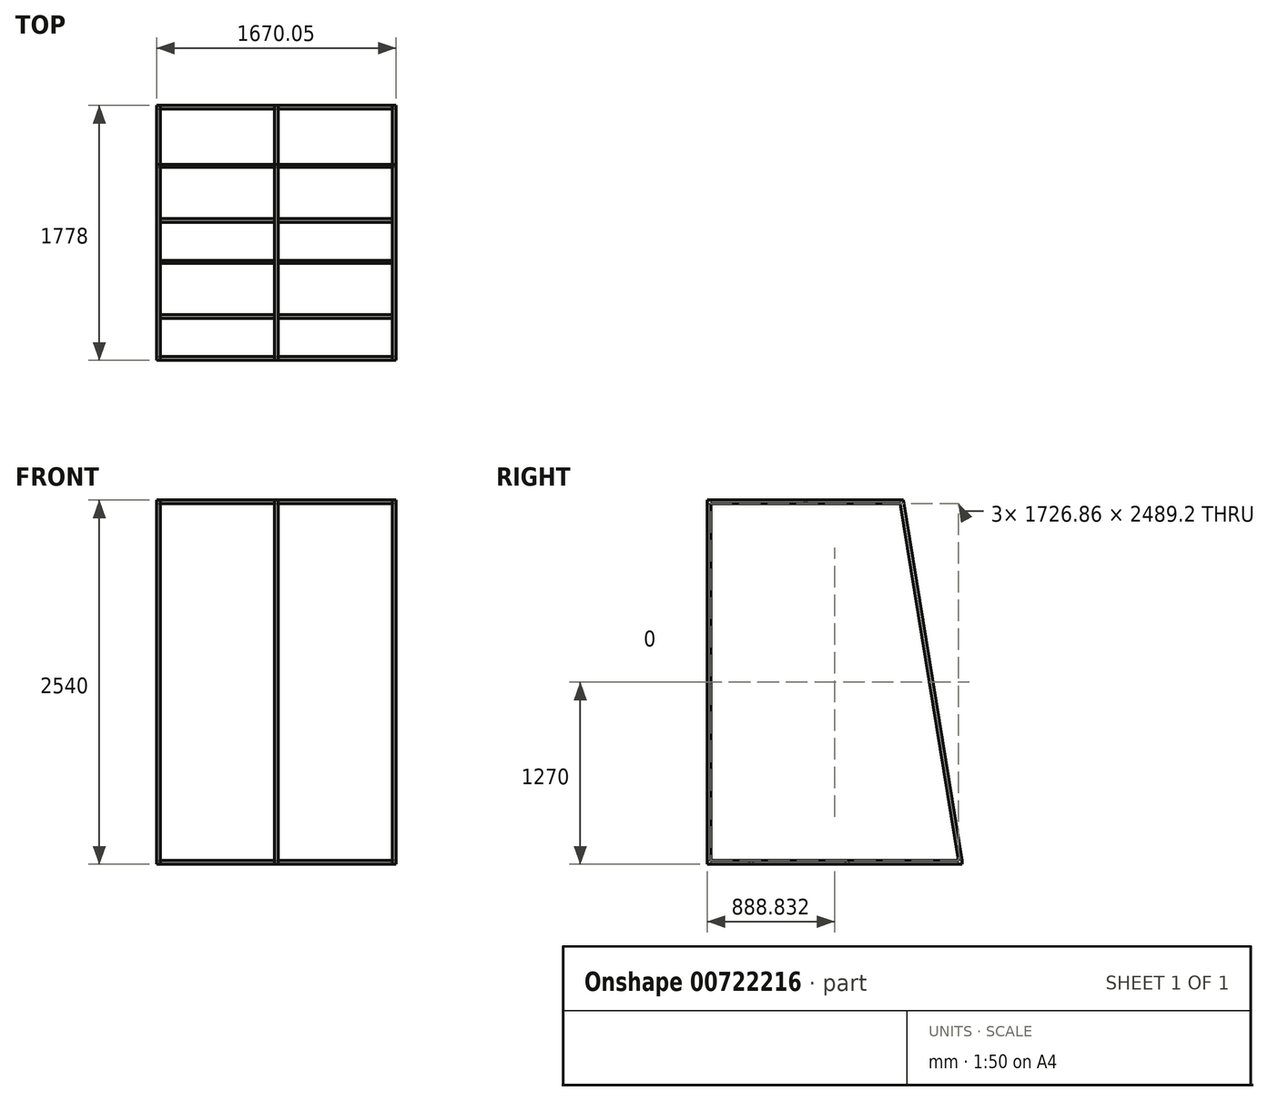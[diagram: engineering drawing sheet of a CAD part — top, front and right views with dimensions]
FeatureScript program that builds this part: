
annotation { "Feature Type Name" : "Feature", "Feature Type Description" : "" }
export const myFeature = defineFeature(function(context is Context, id is Id, definition is map)
    precondition{}
    {
        {
            var Q0;
            Q0=qCreatedBy(makeId("Right.planeOp"),FACE);
            var sketch = newSketch(context, id + "F0", { "sketchPlane" : qUnion([Q0])});
            skLineSegment(sketch, "E0.bottom", {"start": v(0, 0) * mm, "end": v(25.4, 0) * mm});
            skLineSegment(sketch, "E0.top", {"start": v(0, 2489.2) * mm, "end": v(25.4, 2489.2) * mm});
            skLineSegment(sketch, "E0.left", {"start": v(0, 0) * mm, "end": v(0, 2489.2) * mm});
            skLineSegment(sketch, "E0.right", {"start": v(25.4, 0) * mm, "end": v(25.4, 2489.2) * mm});
            skLineSegment(sketch, "E1.bottom", {"start": v(0, 0) * mm, "end": v(1778, 0) * mm});
            skLineSegment(sketch, "E1.top", {"start": v(0, -25.4) * mm, "end": v(1778, -25.4) * mm});
            skLineSegment(sketch, "E1.left", {"start": v(0, 0) * mm, "end": v(0, -25.4) * mm});
            skLineSegment(sketch, "E1.right", {"start": v(1778, 0) * mm, "end": v(1778, -25.4) * mm});
            skLineSegment(sketch, "E2.bottom", {"start": v(0, 2489.2) * mm, "end": v(1371.6, 2489.2) * mm});
            skLineSegment(sketch, "E2.top", {"start": v(0, 2514.6) * mm, "end": v(1367.45, 2514.6) * mm});
            skLineSegment(sketch, "E2.left", {"start": v(0, 2489.2) * mm, "end": v(0, 2514.6) * mm});
            skLineSegment(sketch, "E3", {"start": v(1778, 0) * mm, "end": v(1367.45, 2514.6) * mm});
            skLineSegment(sketch, "E4.0", {"start": v(1752.26, 0) * mm, "end": v(1345.86, 2489.2) * mm});
            skLineSegment(sketch, "E5.bottom", {"start": v(673.1, 2489.2) * mm, "end": v(698.5, 2489.2) * mm});
            skLineSegment(sketch, "E5.top", {"start": v(673.1, 0) * mm, "end": v(698.5, 0) * mm});
            skLineSegment(sketch, "E5.left", {"start": v(673.1, 2489.2) * mm, "end": v(673.1, 0) * mm});
            skLineSegment(sketch, "E5.right", {"start": v(698.5, 2489.2) * mm, "end": v(698.5, 0) * mm});
            skSolve(sketch);
        }
        {
            var Q0;
            Q0 = qSketchRegion(id + "F0", true);
            var Q1;
            Q1=makeQuery(id+"F0.imprint","IMPRINT",FACE,{"disambiguationData":[TD([[makeQuery(id+"F0.imprint","IMPRINT",EDGE,{"derivedFrom":sQuery(id+"F0.wireOp",EDGE,"E5.bottom")}),-1.0]])]});
            extrude(context, id + "F1", {"entities" : qUnion([Q0, Q1]), "depth" : 25.4 * mm, "offsetDistance" : 25.4 * mm});
        }
        {
            var Q0;
            Q0=makeQuery(id+"F1.opExtrude","CAP_FACE",FACE,{"disambiguationData":[OSD([sQuery(id+"F0.wireOp",EDGE,"E0.left"),sQuery(id+"F0.wireOp",EDGE,"E0.right"),sQuery(id+"F0.wireOp",EDGE,"E1.bottom"),sQuery(id+"F0.wireOp",EDGE,"E1.top"),sQuery(id+"F0.wireOp",EDGE,"E1.left"),sQuery(id+"F0.wireOp",EDGE,"E1.right"),sQuery(id+"F0.wireOp",EDGE,"E2.bottom"),sQuery(id+"F0.wireOp",EDGE,"E2.top"),sQuery(id+"F0.wireOp",EDGE,"E2.left"),sQuery(id+"F0.wireOp",EDGE,"E3"),sQuery(id+"F0.wireOp",EDGE,"E4.0"),sQuery(id+"F0.wireOp",EDGE,"E5.left"),sQuery(id+"F0.wireOp",EDGE,"E5.right")])],"isStart":false});
            cPlane(context, id + "F2", {"entities" : qUnion([Q0]), "cplaneType" : CPlaneType.OFFSET, "offset" : 835.02 * mm, "oppositeDirection" : true, "width" : 152.4 * mm, "height" : 152.4 * mm});
        }
        {
            var Q0;
            Q0=makeQuery(id+"F1.opExtrude","SWEPT_BODY",BODY,{"disambiguationData":[OSD([sQuery(id+"F0.wireOp",EDGE,"E0.left"),sQuery(id+"F0.wireOp",EDGE,"E0.right"),sQuery(id+"F0.wireOp",EDGE,"E1.bottom"),sQuery(id+"F0.wireOp",EDGE,"E1.top"),sQuery(id+"F0.wireOp",EDGE,"E1.left"),sQuery(id+"F0.wireOp",EDGE,"E1.right"),sQuery(id+"F0.wireOp",EDGE,"E2.bottom"),sQuery(id+"F0.wireOp",EDGE,"E2.top"),sQuery(id+"F0.wireOp",EDGE,"E2.left"),sQuery(id+"F0.wireOp",EDGE,"E3"),sQuery(id+"F0.wireOp",EDGE,"E4.0"),sQuery(id+"F0.wireOp",EDGE,"E5.left"),sQuery(id+"F0.wireOp",EDGE,"E5.right")])]});
            var Q1;
            Q1=qCreatedBy(id+"F2.planeOp",FACE);
            mirror(context, id + "F3", {"entities" : qUnion([Q0]), "mirrorPlane" : qUnion([Q1])});
        }
        {
            var Q0;
            Q0=makeQuery(id+"F1.opExtrude","CAP_FACE",FACE,{"disambiguationData":[OSD([sQuery(id+"F0.wireOp",EDGE,"E0.left"),sQuery(id+"F0.wireOp",EDGE,"E0.right"),sQuery(id+"F0.wireOp",EDGE,"E1.bottom"),sQuery(id+"F0.wireOp",EDGE,"E1.top"),sQuery(id+"F0.wireOp",EDGE,"E1.left"),sQuery(id+"F0.wireOp",EDGE,"E1.right"),sQuery(id+"F0.wireOp",EDGE,"E2.bottom"),sQuery(id+"F0.wireOp",EDGE,"E2.top"),sQuery(id+"F0.wireOp",EDGE,"E2.left"),sQuery(id+"F0.wireOp",EDGE,"E3"),sQuery(id+"F0.wireOp",EDGE,"E4.0"),sQuery(id+"F0.wireOp",EDGE,"E5.left"),sQuery(id+"F0.wireOp",EDGE,"E5.right")])],"isStart":false});
            cPlane(context, id + "F4", {"entities" : qUnion([Q0]), "cplaneType" : CPlaneType.OFFSET, "offset" : 423.86 * mm, "oppositeDirection" : true, "width" : 152.4 * mm, "height" : 152.4 * mm});
        }
        {
            var Q0;
            Q0=makeQuery(id+"F1.opExtrude","SWEPT_BODY",BODY,{"disambiguationData":[OSD([sQuery(id+"F0.wireOp",EDGE,"E0.left"),sQuery(id+"F0.wireOp",EDGE,"E0.right"),sQuery(id+"F0.wireOp",EDGE,"E1.bottom"),sQuery(id+"F0.wireOp",EDGE,"E1.top"),sQuery(id+"F0.wireOp",EDGE,"E1.left"),sQuery(id+"F0.wireOp",EDGE,"E1.right"),sQuery(id+"F0.wireOp",EDGE,"E2.bottom"),sQuery(id+"F0.wireOp",EDGE,"E2.top"),sQuery(id+"F0.wireOp",EDGE,"E2.left"),sQuery(id+"F0.wireOp",EDGE,"E3"),sQuery(id+"F0.wireOp",EDGE,"E4.0"),sQuery(id+"F0.wireOp",EDGE,"E5.left"),sQuery(id+"F0.wireOp",EDGE,"E5.right")])]});
            var Q1;
            Q1=qCreatedBy(id+"F4.planeOp",FACE);
            mirror(context, id + "F5", {"entities" : qUnion([Q0]), "mirrorPlane" : qUnion([Q1])});
        }
        {
            var Q0;
            Q0=makeQuery(id+"F5.opPattern","COPY",FACE,{"derivedFrom":makeQuery(id+"F1.opExtrude","CAP_FACE",FACE,{"disambiguationData":[OSD([sQuery(id+"F0.wireOp",EDGE,"E0.left"),sQuery(id+"F0.wireOp",EDGE,"E0.right"),sQuery(id+"F0.wireOp",EDGE,"E1.bottom"),sQuery(id+"F0.wireOp",EDGE,"E1.top"),sQuery(id+"F0.wireOp",EDGE,"E1.left"),sQuery(id+"F0.wireOp",EDGE,"E1.right"),sQuery(id+"F0.wireOp",EDGE,"E2.bottom"),sQuery(id+"F0.wireOp",EDGE,"E2.top"),sQuery(id+"F0.wireOp",EDGE,"E2.left"),sQuery(id+"F0.wireOp",EDGE,"E3"),sQuery(id+"F0.wireOp",EDGE,"E4.0"),sQuery(id+"F0.wireOp",EDGE,"E5.left"),sQuery(id+"F0.wireOp",EDGE,"E5.right")])],"isStart":true}),"instanceName":"1"});
            var sketch = newSketch(context, id + "F6", { "sketchPlane" : qUnion([Q0])});
            skLineSegment(sketch, "E6.bottom", {"start": v(1778, -25.4) * mm, "end": v(1752.6, -25.4) * mm});
            skLineSegment(sketch, "E6.top", {"start": v(1778, 0) * mm, "end": v(1752.6, 0) * mm});
            skLineSegment(sketch, "E6.left", {"start": v(1778, -25.4) * mm, "end": v(1778, 0) * mm});
            skLineSegment(sketch, "E6.right", {"start": v(1752.6, -25.4) * mm, "end": v(1752.6, 0) * mm});
            skLineSegment(sketch, "E7.bottom", {"start": v(0, -25.4) * mm, "end": v(25.4, -25.4) * mm});
            skLineSegment(sketch, "E7.top", {"start": v(0, 0) * mm, "end": v(25.4, 0) * mm});
            skLineSegment(sketch, "E7.left", {"start": v(0, -25.4) * mm, "end": v(0, 0) * mm});
            skLineSegment(sketch, "E7.right", {"start": v(25.4, -25.4) * mm, "end": v(25.4, 0) * mm});
            skLineSegment(sketch, "E8.bottom", {"start": v(0, 2514.6) * mm, "end": v(25.4, 2514.6) * mm});
            skLineSegment(sketch, "E8.top", {"start": v(0, 2489.2) * mm, "end": v(25.4, 2489.2) * mm});
            skLineSegment(sketch, "E8.left", {"start": v(0, 2514.6) * mm, "end": v(0, 2489.2) * mm});
            skLineSegment(sketch, "E8.right", {"start": v(25.4, 2514.6) * mm, "end": v(25.4, 2489.2) * mm});
            skLineSegment(sketch, "E9.bottom", {"start": v(292.1, 0) * mm, "end": v(317.5, 0) * mm});
            skLineSegment(sketch, "E9.top", {"start": v(292.1, -25.4) * mm, "end": v(317.5, -25.4) * mm});
            skLineSegment(sketch, "E9.left", {"start": v(292.1, 0) * mm, "end": v(292.1, -25.4) * mm});
            skLineSegment(sketch, "E9.right", {"start": v(317.5, 0) * mm, "end": v(317.5, -25.4) * mm});
            skLineSegment(sketch, "E10.bottom", {"start": v(962.03, 0) * mm, "end": v(987.43, 0) * mm});
            skLineSegment(sketch, "E10.top", {"start": v(962.03, -25.4) * mm, "end": v(987.43, -25.4) * mm});
            skLineSegment(sketch, "E10.left", {"start": v(962.03, 0) * mm, "end": v(962.03, -25.4) * mm});
            skLineSegment(sketch, "E10.right", {"start": v(987.43, 0) * mm, "end": v(987.43, -25.4) * mm});
            skPoint(sketch, "E11.centerSnap0", {"position": v(25.4, 2501.9) * mm});
            skLineSegment(sketch, "E12", {"start": v(673.1, 2489.2) * mm, "end": v(698.5, 2489.2) * mm, "construction": true});
            skCircle(sketch, "E13", {"center": v(685.8, 2501.9) * mm, "radius": 12.7 * mm, "construction": true});
            skPoint(sketch, "E13.centerSnap0", {"position": v(685.8, 2489.2) * mm});
            skCircle(sketch, "E14", {"center": v(1355.72, 2501.9) * mm, "radius": 12.7 * mm, "construction": true});
            skCircle(sketch, "E15", {"center": v(685.8, 2501.9) * mm, "radius": 9.53 * mm});
            skCircle(sketch, "E16", {"center": v(1355.72, 2501.9) * mm, "radius": 9.53 * mm});
            skSolve(sketch);
        }
        {
            var Q0;
            Q0 = qSketchRegion(id + "F6", true);
            var Q1;
            Q1=makeQuery(id+"F1.opExtrude","CAP_FACE",FACE,{"disambiguationData":[OSD([sQuery(id+"F0.wireOp",EDGE,"E0.left"),sQuery(id+"F0.wireOp",EDGE,"E0.right"),sQuery(id+"F0.wireOp",EDGE,"E1.bottom"),sQuery(id+"F0.wireOp",EDGE,"E1.top"),sQuery(id+"F0.wireOp",EDGE,"E1.left"),sQuery(id+"F0.wireOp",EDGE,"E1.right"),sQuery(id+"F0.wireOp",EDGE,"E2.bottom"),sQuery(id+"F0.wireOp",EDGE,"E2.top"),sQuery(id+"F0.wireOp",EDGE,"E2.left"),sQuery(id+"F0.wireOp",EDGE,"E3"),sQuery(id+"F0.wireOp",EDGE,"E4.0"),sQuery(id+"F0.wireOp",EDGE,"E5.left"),sQuery(id+"F0.wireOp",EDGE,"E5.right")])],"isStart":true});
            extrude(context, id + "F7", {"entities" : qUnion([Q0]), "endBound" : BoundingType.UP_TO_SURFACE, "depth" : 25.4 * mm, "endBoundEntityFace" : qUnion([Q1]), "offsetDistance" : 25.4 * mm});
        }
        {
            var Q0;
            Q0=makeQuery(id+"F5.opPattern","COPY",FACE,{"derivedFrom":makeQuery(id+"F1.opExtrude","CAP_FACE",FACE,{"disambiguationData":[OSD([sQuery(id+"F0.wireOp",EDGE,"E0.left"),sQuery(id+"F0.wireOp",EDGE,"E0.right"),sQuery(id+"F0.wireOp",EDGE,"E1.bottom"),sQuery(id+"F0.wireOp",EDGE,"E1.top"),sQuery(id+"F0.wireOp",EDGE,"E1.left"),sQuery(id+"F0.wireOp",EDGE,"E1.right"),sQuery(id+"F0.wireOp",EDGE,"E2.bottom"),sQuery(id+"F0.wireOp",EDGE,"E2.top"),sQuery(id+"F0.wireOp",EDGE,"E2.left"),sQuery(id+"F0.wireOp",EDGE,"E3"),sQuery(id+"F0.wireOp",EDGE,"E4.0"),sQuery(id+"F0.wireOp",EDGE,"E5.left"),sQuery(id+"F0.wireOp",EDGE,"E5.right")])],"isStart":true}),"instanceName":"1"});
            cPlane(context, id + "F8", {"entities" : qUnion([Q0]), "cplaneType" : CPlaneType.OFFSET, "offset" : 12.7 * mm, "oppositeDirection" : true, "width" : 152.4 * mm, "height" : 152.4 * mm});
        }
        {
            var Q0;
            Q0=makeQuery(id+"F7.opExtrude","SWEPT_BODY",BODY,{"disambiguationData":[OSD([sQuery(id+"F6.wireOp",EDGE,"E8.bottom"),sQuery(id+"F6.wireOp",EDGE,"E8.top"),sQuery(id+"F6.wireOp",EDGE,"E8.left"),sQuery(id+"F6.wireOp",EDGE,"E8.right")])]});
            var Q1;
            Q1=makeQuery(id+"F7.opExtrude","SWEPT_BODY",BODY,{"disambiguationData":[OSD([sQuery(id+"F6.wireOp",EDGE,"E15")])]});
            var Q2;
            Q2=makeQuery(id+"F7.opExtrude","SWEPT_BODY",BODY,{"disambiguationData":[OSD([sQuery(id+"F6.wireOp",EDGE,"E16")])]});
            var Q3;
            Q3=makeQuery(id+"F7.opExtrude","SWEPT_BODY",BODY,{"disambiguationData":[OSD([sQuery(id+"F6.wireOp",EDGE,"E6.bottom"),sQuery(id+"F6.wireOp",EDGE,"E6.top"),sQuery(id+"F6.wireOp",EDGE,"E6.left"),sQuery(id+"F6.wireOp",EDGE,"E6.right")])]});
            var Q4;
            Q4=makeQuery(id+"F7.opExtrude","SWEPT_BODY",BODY,{"disambiguationData":[OSD([sQuery(id+"F6.wireOp",EDGE,"E10.bottom"),sQuery(id+"F6.wireOp",EDGE,"E10.top"),sQuery(id+"F6.wireOp",EDGE,"E10.left"),sQuery(id+"F6.wireOp",EDGE,"E10.right")])]});
            var Q5;
            Q5=makeQuery(id+"F7.opExtrude","SWEPT_BODY",BODY,{"disambiguationData":[OSD([sQuery(id+"F6.wireOp",EDGE,"E9.bottom"),sQuery(id+"F6.wireOp",EDGE,"E9.top"),sQuery(id+"F6.wireOp",EDGE,"E9.left"),sQuery(id+"F6.wireOp",EDGE,"E9.right")])]});
            var Q6;
            Q6=makeQuery(id+"F7.opExtrude","SWEPT_BODY",BODY,{"disambiguationData":[OSD([sQuery(id+"F6.wireOp",EDGE,"E7.bottom"),sQuery(id+"F6.wireOp",EDGE,"E7.top"),sQuery(id+"F6.wireOp",EDGE,"E7.left"),sQuery(id+"F6.wireOp",EDGE,"E7.right")])]});
            var Q7;
            Q7=qCreatedBy(id+"F8.planeOp",FACE);
            mirror(context, id + "F9", {"entities" : qUnion([Q0, Q1, Q2, Q3, Q4, Q5, Q6]), "mirrorPlane" : qUnion([Q7])});
        }
    });
